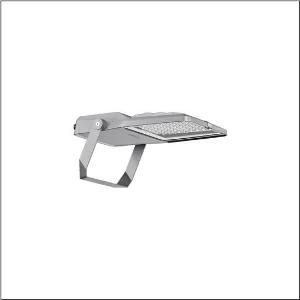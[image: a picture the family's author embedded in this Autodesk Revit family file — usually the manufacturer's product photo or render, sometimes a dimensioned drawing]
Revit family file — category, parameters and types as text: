
# Revit family: floodlight_fl_21_mini___pl33t_5xa7775b2f1a_fedb
name_source: partatom
category: Lighting Fixtures
units: mm (PartAtom-declared; Revit-internal decimal feet)

## family parameters
Cut with Voids When Loaded = No
Host = Face
Light Source = No
Part Type = Normal
Room Calculation Point = No
Round Connector Dimension = Use Diameter
Shared = No

## types (1)
- --- (1 x LED, 6150 lm, 45.7 W, 3000K)
    Apparent Load = 46 VA
    CIE Flux Codes = 26 75 99 100 100
    Color Rendering = 70
    Color Temperature = 3000K
    Default Elevation = 1800 mm
    Description = Floodlight FL 21 mini, floodlight, primary light control with lens, of PMMA, primary optical cover: protective disc, of toughened safety glass, transparent, light distribution: PL33T, light emission: direct distribution, installation type: surface-mounted, LED, High Power LED, rated luminous flux: 6.150lm, luminous efficacy: 135lm/W, light colour: 730, colour temperature: 3000K, control gear: Smart Interface (Zhaga), control: flexible luminous flux parameterisation, time-dependent luminous flux control, constant luminous flux control, overheat protection, pre-setting: logarithmic dimming characteristic, with terminal, 6-pole, mains connection: 220..240V, AC, 50/60Hz, start of lifetime: 46W, end of service life: 48W, reduction: 22W, luminaire housing, of diecast aluminium, powder-coated, SITECO metallic grey (DB 702S), corrosivity category C5 mid according to DIN EN ISO 12944, suitable for swimming pools, chlorine-resistant, sealing non-destructively replaceable, mounting bracket, of steel, galvanised, powder-coated, SITECO metallic grey (DB 702S), Smart Interface above, protection rating (complete): IP66, insulation class (complete): insulation class II (safety insulation), certification: CE, ENEC, VDE, protection symbol: D, impact resistance: IK08, permissible operating ambient temperature: -40..+40°C, permissible operating ambient temperature for outdoor applications: -40..+50°C, standard: DIN EN 12944, LABS conformity tested according to VDMA 24364:2018-05, packaging unit: 1 piece

Light Distribution: PL33T
    Height = 70 mm
    Lamp = 1 x LED
    Lamp Light Flux = 6150 lm
    Lamp Power = 45.7 W
    Lamp count = 1
    Length = 485 mm
    Luminous efficacy = 135 lm/W
    Manufacturer = Siteco
    ModVariant = No
    Model = 5XA7775B2F1A
    Mounting Place = Pole
    Mounting Type = Pole annexe
    Number of Poles = 1
    OnlyDefault = Yes
    Power Factor = 1
    Product Name = Floodlight FL 21 mini | PL33T
    Product group = floodlight | pylon annexe
    ProductGroupID = 6201
    Protection Class = Protection class II
    Protection Degree = IP 66
    RLX_Detail_Level = 1
    RLX_Emergency_Light_Flux = 0 lm
    RLX_Emergency_Type = 0
    RLX_Emergency_Type_DB = No
    RlxData = <blob elided: 95961 chars, md5=3e00335f>
    Socket = socket
    Standby Power = 0 W
    System Light Flux = 6150 lm
    System Power = 46 W
    Type Comments = factory setting: luminous flux: 100 % | dim-lin: 254 | 463 mA
    Type Image = l_1006845.jpg
    URL = http://relux.com
    VarID = @adj_149759
    Voltage = 0 V
    Weight = 0.00 kg
    Width = 337 mm

## geometry (parser evidence)
native form markers: Blend x4, Sweep x12
no freeform markers — native parametric forms only
